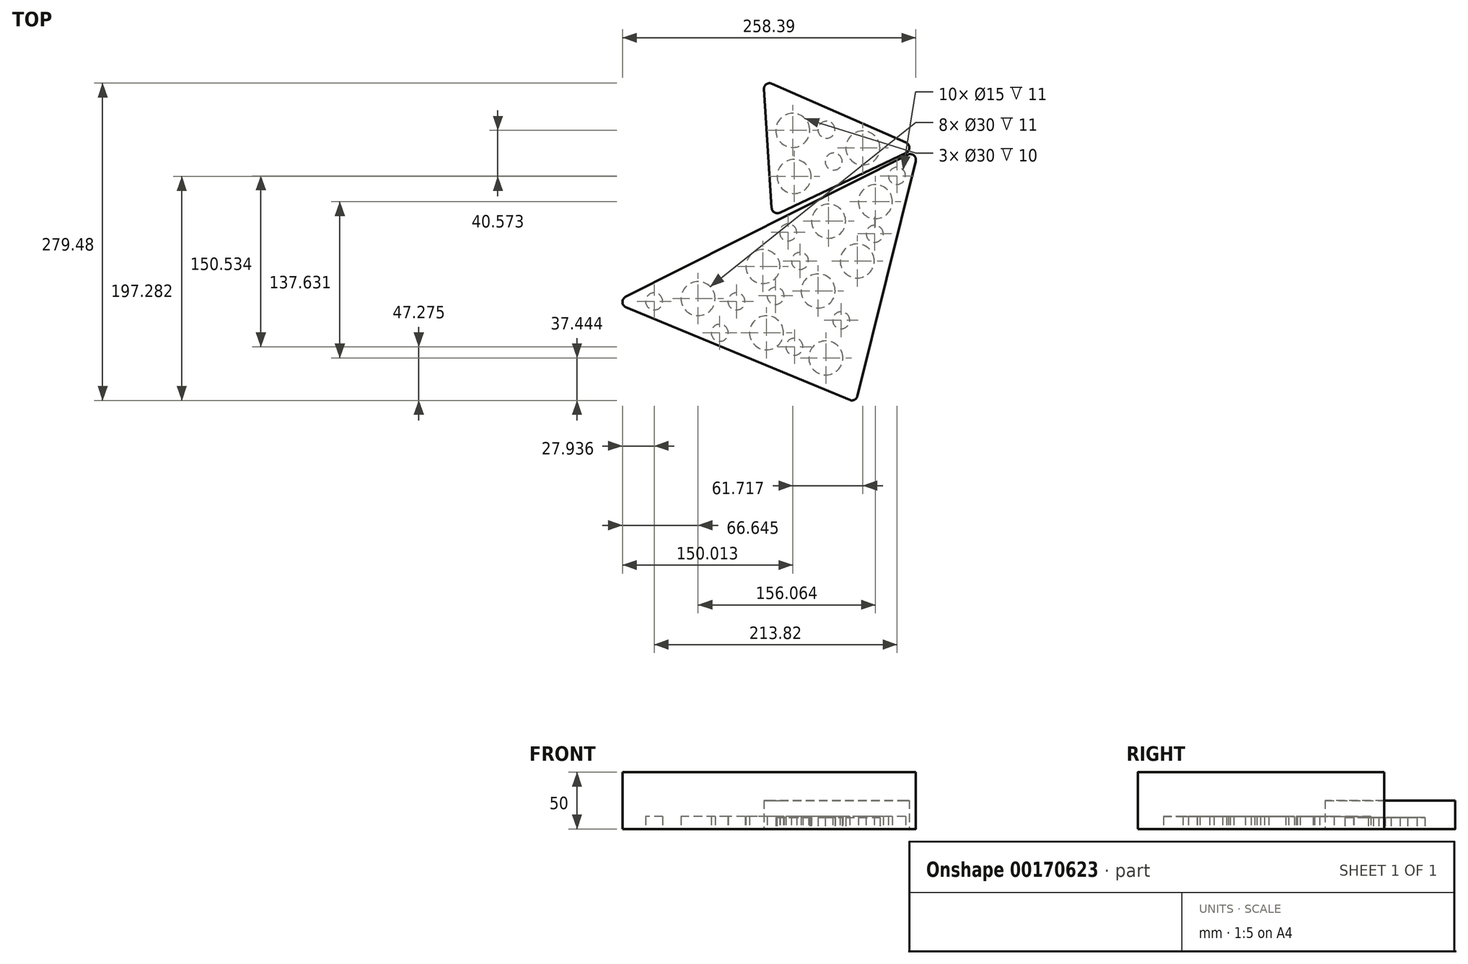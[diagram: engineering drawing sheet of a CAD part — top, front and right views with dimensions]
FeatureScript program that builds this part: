
annotation { "Feature Type Name" : "Feature", "Feature Type Description" : "" }
export const myFeature = defineFeature(function(context is Context, id is Id, definition is map)
    precondition{}
    {
        {
            var Q0;
            Q0=qCreatedBy(makeId("Top.planeOp"),FACE);
            var sketch = newSketch(context, id + "F0", { "sketchPlane" : qUnion([Q0])});
            skLineSegment(sketch, "E0", {"start": v(-169.25, -54.17) * mm, "end": v(98.6, 80.95) * mm});
            skLineSegment(sketch, "E1", {"start": v(98.6, 80.95) * mm, "end": v(43.2, -142.28) * mm});
            skLineSegment(sketch, "E2", {"start": v(43.2, -142.28) * mm, "end": v(-169.25, -54.17) * mm});
            skSolve(sketch);
        }
        {
            var Q0;
            Q0=makeQuery(id+"F0.imprint","IMPRINT",FACE,{"disambiguationData":[TD([[makeQuery(id+"F0.imprint","IMPRINT",EDGE,{"derivedFrom":sQuery(id+"F0.wireOp",EDGE,"E0")}),-1.0]])]});
            extrude(context, id + "F1", {"entities" : qUnion([Q0]), "depth" : 50 * mm});
        }
        {
            var Q0;
            Q0=qCreatedBy(makeId("Top.planeOp"),FACE);
            var sketch = newSketch(context, id + "F2", { "sketchPlane" : qUnion([Q0])});
            skCircle(sketch, "E3", {"center": v(-95.63, -50.76) * mm, "radius": 15 * mm});
            skCircle(sketch, "E4", {"center": v(-38.48, -22.5) * mm, "radius": 15 * mm});
            skCircle(sketch, "E5", {"center": v(-35.41, -80.87) * mm, "radius": 15 * mm});
            skCircle(sketch, "E6", {"center": v(16.81, -102.99) * mm, "radius": 15 * mm});
            skCircle(sketch, "E7", {"center": v(10.06, -44) * mm, "radius": 15 * mm});
            skCircle(sketch, "E8", {"center": v(44.46, -17.58) * mm, "radius": 15 * mm});
            skCircle(sketch, "E9", {"center": v(19.27, 17.44) * mm, "radius": 15 * mm});
            skCircle(sketch, "E10", {"center": v(60.44, 34.65) * mm, "radius": 15 * mm});
            skCircle(sketch, "E11", {"center": v(-61.83, -53.22) * mm, "radius": 7.5 * mm});
            skCircle(sketch, "E12", {"center": v(-27.42, -48.3) * mm, "radius": 7.5 * mm});
            skCircle(sketch, "E13", {"center": v(-16.36, 7.61) * mm, "radius": 7.5 * mm});
            skCircle(sketch, "E14", {"center": v(-134.33, -53.22) * mm, "radius": 7.5 * mm});
            skCircle(sketch, "E15", {"center": v(30.33, -69.8) * mm, "radius": 7.5 * mm});
            skCircle(sketch, "E16", {"center": v(-10.83, -93.15) * mm, "radius": 7.5 * mm});
            skCircle(sketch, "E17", {"center": v(-76.58, -80.87) * mm, "radius": 7.5 * mm});
            skCircle(sketch, "E18", {"center": v(-5.92, -17.58) * mm, "radius": 7.5 * mm});
            skCircle(sketch, "E19", {"center": v(59.82, 6.38) * mm, "radius": 7.5 * mm});
            skCircle(sketch, "E20", {"center": v(79.49, 57.38) * mm, "radius": 7.5 * mm});
            skSolve(sketch);
        }
        {
            var Q0;
            Q0=makeQuery(id+"F2.imprint","IMPRINT",FACE,{"disambiguationData":[TD([[makeQuery(id+"F2.imprint","IMPRINT",EDGE,{"derivedFrom":sQuery(id+"F2.wireOp",EDGE,"E3")}),1.0]])]});
            var Q1;
            Q1=makeQuery(id+"F2.imprint","IMPRINT",FACE,{"disambiguationData":[TD([[makeQuery(id+"F2.imprint","IMPRINT",EDGE,{"derivedFrom":sQuery(id+"F2.wireOp",EDGE,"E17")}),1.0]])]});
            var Q2;
            Q2=makeQuery(id+"F2.imprint","IMPRINT",FACE,{"disambiguationData":[TD([[makeQuery(id+"F2.imprint","IMPRINT",EDGE,{"derivedFrom":sQuery(id+"F2.wireOp",EDGE,"E14")}),1.0]])]});
            var Q3;
            Q3=makeQuery(id+"F2.imprint","IMPRINT",FACE,{"disambiguationData":[TD([[makeQuery(id+"F2.imprint","IMPRINT",EDGE,{"derivedFrom":sQuery(id+"F2.wireOp",EDGE,"E4")}),1.0]])]});
            var Q4;
            Q4=makeQuery(id+"F2.imprint","IMPRINT",FACE,{"disambiguationData":[TD([[makeQuery(id+"F2.imprint","IMPRINT",EDGE,{"derivedFrom":sQuery(id+"F2.wireOp",EDGE,"E5")}),1.0]])]});
            var Q5;
            Q5=makeQuery(id+"F2.imprint","IMPRINT",FACE,{"disambiguationData":[TD([[makeQuery(id+"F2.imprint","IMPRINT",EDGE,{"derivedFrom":sQuery(id+"F2.wireOp",EDGE,"E11")}),1.0]])]});
            var Q6;
            Q6=makeQuery(id+"F2.imprint","IMPRINT",FACE,{"disambiguationData":[TD([[makeQuery(id+"F2.imprint","IMPRINT",EDGE,{"derivedFrom":sQuery(id+"F2.wireOp",EDGE,"E12")}),1.0]])]});
            var Q7;
            Q7=makeQuery(id+"F2.imprint","IMPRINT",FACE,{"disambiguationData":[TD([[makeQuery(id+"F2.imprint","IMPRINT",EDGE,{"derivedFrom":sQuery(id+"F2.wireOp",EDGE,"E16")}),1.0]])]});
            var Q8;
            Q8=makeQuery(id+"F2.imprint","IMPRINT",FACE,{"disambiguationData":[TD([[makeQuery(id+"F2.imprint","IMPRINT",EDGE,{"derivedFrom":sQuery(id+"F2.wireOp",EDGE,"E18")}),1.0]])]});
            var Q9;
            Q9=makeQuery(id+"F2.imprint","IMPRINT",FACE,{"disambiguationData":[TD([[makeQuery(id+"F2.imprint","IMPRINT",EDGE,{"derivedFrom":sQuery(id+"F2.wireOp",EDGE,"E13")}),1.0]])]});
            var Q10;
            Q10=makeQuery(id+"F2.imprint","IMPRINT",FACE,{"disambiguationData":[TD([[makeQuery(id+"F2.imprint","IMPRINT",EDGE,{"derivedFrom":sQuery(id+"F2.wireOp",EDGE,"E7")}),1.0]])]});
            var Q11;
            Q11=makeQuery(id+"F2.imprint","IMPRINT",FACE,{"disambiguationData":[TD([[makeQuery(id+"F2.imprint","IMPRINT",EDGE,{"derivedFrom":sQuery(id+"F2.wireOp",EDGE,"E6")}),1.0]])]});
            var Q12;
            Q12=makeQuery(id+"F2.imprint","IMPRINT",FACE,{"disambiguationData":[TD([[makeQuery(id+"F2.imprint","IMPRINT",EDGE,{"derivedFrom":sQuery(id+"F2.wireOp",EDGE,"E15")}),1.0]])]});
            var Q13;
            Q13=makeQuery(id+"F2.imprint","IMPRINT",FACE,{"disambiguationData":[TD([[makeQuery(id+"F2.imprint","IMPRINT",EDGE,{"derivedFrom":sQuery(id+"F2.wireOp",EDGE,"E8")}),1.0]])]});
            var Q14;
            Q14=makeQuery(id+"F2.imprint","IMPRINT",FACE,{"disambiguationData":[TD([[makeQuery(id+"F2.imprint","IMPRINT",EDGE,{"derivedFrom":sQuery(id+"F2.wireOp",EDGE,"E9")}),1.0]])]});
            var Q15;
            Q15=makeQuery(id+"F2.imprint","IMPRINT",FACE,{"disambiguationData":[TD([[makeQuery(id+"F2.imprint","IMPRINT",EDGE,{"derivedFrom":sQuery(id+"F2.wireOp",EDGE,"E10")}),1.0]])]});
            var Q16;
            Q16=makeQuery(id+"F2.imprint","IMPRINT",FACE,{"disambiguationData":[TD([[makeQuery(id+"F2.imprint","IMPRINT",EDGE,{"derivedFrom":sQuery(id+"F2.wireOp",EDGE,"E19")}),1.0]])]});
            var Q17;
            Q17=makeQuery(id+"F2.imprint","IMPRINT",FACE,{"disambiguationData":[TD([[makeQuery(id+"F2.imprint","IMPRINT",EDGE,{"derivedFrom":sQuery(id+"F2.wireOp",EDGE,"E20")}),1.0]])]});
            var Q18;
            Q18=sQuery(id+"F2.wireOp",EDGE,"E3");
            var Q19;
            Q19=sQuery(id+"F2.wireOp",EDGE,"E14");
            var Q20;
            Q20=sQuery(id+"F2.wireOp",EDGE,"E17");
            var Q21;
            Q21=sQuery(id+"F2.wireOp",EDGE,"E11");
            var Q22;
            Q22=sQuery(id+"F2.wireOp",EDGE,"E4");
            var Q23;
            Q23=sQuery(id+"F2.wireOp",EDGE,"E5");
            var Q24;
            Q24=sQuery(id+"F2.wireOp",EDGE,"E12");
            var Q25;
            Q25=sQuery(id+"F2.wireOp",EDGE,"E16");
            var Q26;
            Q26=sQuery(id+"F2.wireOp",EDGE,"E6");
            var Q27;
            Q27=sQuery(id+"F2.wireOp",EDGE,"E15");
            var Q28;
            Q28=sQuery(id+"F2.wireOp",EDGE,"E7");
            var Q29;
            Q29=sQuery(id+"F2.wireOp",EDGE,"E18");
            var Q30;
            Q30=sQuery(id+"F2.wireOp",EDGE,"E13");
            var Q31;
            Q31=sQuery(id+"F2.wireOp",EDGE,"E9");
            var Q32;
            Q32=sQuery(id+"F2.wireOp",EDGE,"E8");
            var Q33;
            Q33=sQuery(id+"F2.wireOp",EDGE,"E19");
            var Q34;
            Q34=sQuery(id+"F2.wireOp",EDGE,"E10");
            var Q35;
            Q35=sQuery(id+"F2.wireOp",EDGE,"E20");
            extrude(context, id + "F3", {"entities" : qUnion([Q0, Q1, Q2, Q3, Q4, Q5, Q6, Q7, Q8, Q9, Q10, Q11, Q12, Q13, Q14, Q15, Q16, Q17]), "operationType" : NewBodyOperationType.REMOVE, "surfaceEntities" : qUnion([Q18, Q19, Q20, Q21, Q22, Q23, Q24, Q25, Q26, Q27, Q28, Q29, Q30, Q31, Q32, Q33, Q34, Q35]), "depth" : 11 * mm});
        }
        {
            var Q0;
            Q0=qCreatedBy(makeId("Top.planeOp"),FACE);
            var sketch = newSketch(context, id + "F4", { "sketchPlane" : qUnion([Q0])});
            skLineSegment(sketch, "E21", {"start": v(-30.39, 21.82) * mm, "end": v(97.4, 82.27) * mm});
            skLineSegment(sketch, "E22", {"start": v(97.4, 82.27) * mm, "end": v(-38.16, 141.95) * mm});
            skLineSegment(sketch, "E23", {"start": v(-38.16, 141.95) * mm, "end": v(-30.39, 21.82) * mm});
            skSolve(sketch);
        }
        {
            var Q0;
            Q0 = qSketchRegion(id + "F4", true);
            extrude(context, id + "F5", {"entities" : qUnion([Q0]), "depth" : 25 * mm});
        }
        {
            var Q0;
            Q0=makeQuery(id+"F5.opExtrude","CAP_FACE",FACE,{"disambiguationData":[OSD([sQuery(id+"F4.wireOp",EDGE,"E21"),sQuery(id+"F4.wireOp",EDGE,"E22"),sQuery(id+"F4.wireOp",EDGE,"E23")])],"isStart":true});
            var sketch = newSketch(context, id + "F6", { "sketchPlane" : qUnion([Q0])});
            skCircle(sketch, "E24", {"center": v(-11.11, -56.85) * mm, "radius": 15 * mm});
            skCircle(sketch, "E25", {"center": v(23.74, -70) * mm, "radius": 7.5 * mm});
            skCircle(sketch, "E26", {"center": v(-12.26, -97.42) * mm, "radius": 15 * mm});
            skCircle(sketch, "E27", {"center": v(17.46, -98) * mm, "radius": 7.5 * mm});
            skCircle(sketch, "E28", {"center": v(49.46, -82) * mm, "radius": 15 * mm});
            skSolve(sketch);
        }
        {
            var Q0;
            Q0=makeQuery(id+"F6.imprint","IMPRINT",FACE,{"disambiguationData":[TD([[makeQuery(id+"F6.imprint","IMPRINT",EDGE,{"derivedFrom":sQuery(id+"F6.wireOp",EDGE,"E24")}),1.0]])]});
            var Q1;
            Q1=makeQuery(id+"F6.imprint","IMPRINT",FACE,{"disambiguationData":[TD([[makeQuery(id+"F6.imprint","IMPRINT",EDGE,{"derivedFrom":sQuery(id+"F6.wireOp",EDGE,"E25")}),1.0]])]});
            var Q2;
            Q2=makeQuery(id+"F6.imprint","IMPRINT",FACE,{"disambiguationData":[TD([[makeQuery(id+"F6.imprint","IMPRINT",EDGE,{"derivedFrom":sQuery(id+"F6.wireOp",EDGE,"E28")}),1.0]])]});
            var Q3;
            Q3=makeQuery(id+"F6.imprint","IMPRINT",FACE,{"disambiguationData":[TD([[makeQuery(id+"F6.imprint","IMPRINT",EDGE,{"derivedFrom":sQuery(id+"F6.wireOp",EDGE,"E27")}),1.0]])]});
            var Q4;
            Q4=makeQuery(id+"F6.imprint","IMPRINT",FACE,{"disambiguationData":[TD([[makeQuery(id+"F6.imprint","IMPRINT",EDGE,{"derivedFrom":sQuery(id+"F6.wireOp",EDGE,"E26")}),1.0]])]});
            extrude(context, id + "F7", {"entities" : qUnion([Q0, Q1, Q2, Q3, Q4]), "operationType" : NewBodyOperationType.REMOVE, "oppositeDirection" : true, "depth" : 10 * mm});
        }
        {
            var Q0;
            Q0=makeQuery(id+"F1.opExtrude","SWEPT_EDGE",EDGE,{"disambiguationData":[OSD([sQuery(id+"F0.wireOp",EDGE,"E0"),sQuery(id+"F0.wireOp",EDGE,"E2")])]});
            var Q1;
            Q1=makeQuery(id+"F5.opExtrude","SWEPT_EDGE",EDGE,{"disambiguationData":[OSD([sQuery(id+"F4.wireOp",EDGE,"E22"),sQuery(id+"F4.wireOp",EDGE,"E23")])]});
            var Q2;
            Q2=makeQuery(id+"F1.opExtrude","SWEPT_EDGE",EDGE,{"disambiguationData":[OSD([sQuery(id+"F0.wireOp",EDGE,"E0"),sQuery(id+"F0.wireOp",EDGE,"E1")])]});
            var Q3;
            Q3=makeQuery(id+"F5.opExtrude","SWEPT_EDGE",EDGE,{"disambiguationData":[OSD([sQuery(id+"F4.wireOp",EDGE,"E21"),sQuery(id+"F4.wireOp",EDGE,"E22")])]});
            var Q4;
            Q4=makeQuery(id+"F1.opExtrude","SWEPT_EDGE",EDGE,{"disambiguationData":[OSD([sQuery(id+"F0.wireOp",EDGE,"E1"),sQuery(id+"F0.wireOp",EDGE,"E2")])]});
            var Q5;
            Q5=makeQuery(id+"F5.opExtrude","SWEPT_EDGE",EDGE,{"disambiguationData":[OSD([sQuery(id+"F4.wireOp",EDGE,"E21"),sQuery(id+"F4.wireOp",EDGE,"E23")])]});
            fillet(context, id + "F8", {"entities" : qUnion([Q0, Q1, Q2, Q3, Q4, Q5]), "radius" : 5 * mm, "tangentPropagation" : true, "allowEdgeOverflow" : false});
        }
    });
